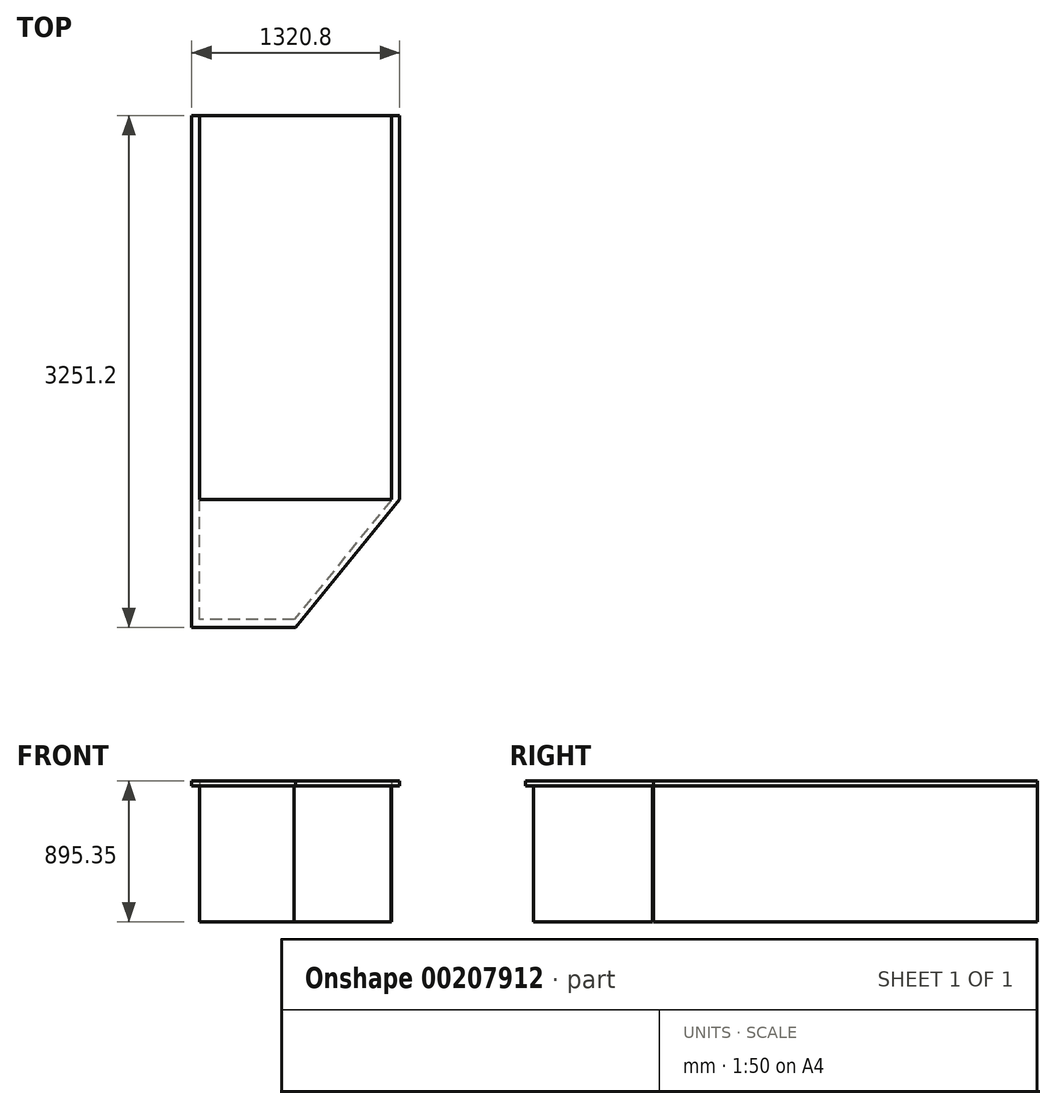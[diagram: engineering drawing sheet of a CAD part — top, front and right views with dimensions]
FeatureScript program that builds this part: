
annotation { "Feature Type Name" : "Feature", "Feature Type Description" : "" }
export const myFeature = defineFeature(function(context is Context, id is Id, definition is map)
    precondition{}
    {
        {
            var Q0;
            Q0=qCreatedBy(makeId("Top.planeOp"),FACE);
            var sketch = newSketch(context, id + "F0", { "sketchPlane" : qUnion([Q0])});
            skLineSegment(sketch, "E0.bottom", {"start": v(0, 0) * mm, "end": v(-1219.2, 0) * mm});
            skLineSegment(sketch, "E0.top", {"start": v(0, -2438.4) * mm, "end": v(-1219.2, -2438.4) * mm});
            skLineSegment(sketch, "E0.left", {"start": v(0, 0) * mm, "end": v(0, -2438.4) * mm});
            skLineSegment(sketch, "E0.right", {"start": v(-1219.2, 0) * mm, "end": v(-1219.2, -2438.4) * mm});
            skSolve(sketch);
        }
        {
            var Q0;
            Q0=makeQuery(id+"F0.imprint","IMPRINT",FACE,{"disambiguationData":[TD([[makeQuery(id+"F0.imprint","IMPRINT",EDGE,{"derivedFrom":sQuery(id+"F0.wireOp",EDGE,"E0.bottom")}),1.0]])]});
            extrude(context, id + "F1", {"entities" : qUnion([Q0]), "depth" : 863.6 * mm});
        }
        {
            var Q0;
            Q0=makeQuery(id+"F1.opExtrude","CAP_FACE",FACE,{"disambiguationData":[OSD([sQuery(id+"F0.wireOp",EDGE,"E0.bottom"),sQuery(id+"F0.wireOp",EDGE,"E0.top"),sQuery(id+"F0.wireOp",EDGE,"E0.left"),sQuery(id+"F0.wireOp",EDGE,"E0.right")])],"isStart":false});
            var sketch = newSketch(context, id + "F2", { "sketchPlane" : qUnion([Q0])});
            skLineSegment(sketch, "E1.bottom", {"start": v(-1270, 0) * mm, "end": v(50.8, 0) * mm});
            skLineSegment(sketch, "E1.top", {"start": v(-1270, -2438.4) * mm, "end": v(50.8, -2438.4) * mm});
            skLineSegment(sketch, "E1.left", {"start": v(-1270, 0) * mm, "end": v(-1270, -2438.4) * mm});
            skLineSegment(sketch, "E1.right", {"start": v(50.8, 0) * mm, "end": v(50.8, -2438.4) * mm});
            skLineSegment(sketch, "E2", {"start": v(-1270, -2438.4) * mm, "end": v(-1270, -3251.2) * mm});
            skLineSegment(sketch, "E3", {"start": v(-1270, -3251.2) * mm, "end": v(-609.6, -3251.2) * mm});
            skPoint(sketch, "E3.endSnap0", {"position": v(-609.6, -2438.4) * mm});
            skLineSegment(sketch, "E4", {"start": v(-609.6, -3251.2) * mm, "end": v(50.8, -2438.4) * mm});
            skSolve(sketch);
        }
        {
            var Q0;
            Q0=makeQuery(id+"F2.imprint","IMPRINT",FACE,{"disambiguationData":[TD([[makeQuery(id+"F2.imprint","IMPRINT",EDGE,{"derivedFrom":sQuery(id+"F2.wireOp",EDGE,"E1.top")}),1.0]])]});
            var Q1;
            Q1=makeQuery(id+"F2.imprint","IMPRINT",FACE,{"disambiguationData":[TD([[makeQuery(id+"F2.imprint","IMPRINT",EDGE,{"derivedFrom":makeQuery(id+"F1.opExtrude","CAP_EDGE",EDGE,{"disambiguationData":[OSD([sQuery(id+"F0.wireOp",EDGE,"E0.top")])],"isStart":false})}),-1.0]])]});
            var Q2;
            Q2=makeQuery(id+"F2.imprint","IMPRINT",FACE,{"disambiguationData":[TD([[makeQuery(id+"F2.imprint","IMPRINT",EDGE,{"derivedFrom":sQuery(id+"F2.wireOp",EDGE,"E1.top")}),-1.0]])]});
            extrude(context, id + "F3", {"entities" : qUnion([Q0, Q1, Q2]), "operationType" : NewBodyOperationType.ADD, "depth" : 31.75 * mm});
        }
        {
            var Q0;
            {var subQ4=sQuery(id+"F2.wireOp",EDGE,"E2");Q0=makeQuery(id+"F2.imprint","IMPRINT",FACE,{"disambiguationData":[TD([[makeQuery(id+"F2.imprint","IMPRINT",EDGE,{"derivedFrom":subQ4}),1.0]])]});}
            var sketch = newSketch(context, id + "F4", { "sketchPlane" : qUnion([Q0])});
            skLineSegment(sketch, "E5", {"start": v(0, -2438.4) * mm, "end": v(-619.12, -3200.4) * mm});
            skLineSegment(sketch, "E6", {"start": v(-619.12, -3200.4) * mm, "end": v(-1219.2, -3200.4) * mm});
            skLineSegment(sketch, "E7", {"start": v(-1219.2, -3200.4) * mm, "end": v(-1219.2, -2438.4) * mm});
            skLineSegment(sketch, "E8", {"start": v(-1219.2, -2438.4) * mm, "end": v(0, -2438.4) * mm});
            skLineSegment(sketch, "E9.0", {"start": v(0, -2444.75) * mm, "end": v(-1219.2, -2444.75) * mm});
            skLineSegment(sketch, "E9.1", {"start": v(-1263.65, -2444.75) * mm, "end": v(-1263.65, -3244.85) * mm});
            skLineSegment(sketch, "E9.2", {"start": v(-1263.65, -3244.85) * mm, "end": v(-612.62, -3244.85) * mm});
            skLineSegment(sketch, "E9.3", {"start": v(-1219.2, -2444.75) * mm, "end": v(-1263.65, -2444.75) * mm});
            skLineSegment(sketch, "E9.4", {"start": v(-612.62, -3244.85) * mm, "end": v(37.46, -2444.75) * mm});
            skLineSegment(sketch, "E9.5", {"start": v(37.46, -2444.75) * mm, "end": v(0, -2444.75) * mm});
            skSolve(sketch);
        }
        {
            var Q0;
            {var subQ1=makeQuery(id+"F1.opExtrude","CAP_EDGE",EDGE,{"disambiguationData":[OSD([sQuery(id+"F0.wireOp",EDGE,"E0.left")])],"isStart":false});Q0=makeQuery(id+"F2.imprint","IMPRINT",FACE,{"disambiguationData":[TD([[makeQuery(id+"F2.imprint","IMPRINT",EDGE,{"derivedFrom":subQ1}),-1.0]])]});}
            extrude(context, id + "F5", {"entities" : qUnion([Q0]), "depth" : 31.75 * mm});
        }
        {
            var Q0;
            {var subQ0=sQuery(id+"F4.wireOp",EDGE,"E6");Q0=makeQuery(id+"F4.imprint","IMPRINT",FACE,{"disambiguationData":[TD([[makeQuery(id+"F4.imprint","IMPRINT",EDGE,{"derivedFrom":subQ0}),-1.0]])]});}
            extrude(context, id + "F6", {"entities" : qUnion([Q0]), "operationType" : NewBodyOperationType.ADD, "oppositeDirection" : true, "depth" : 863.6 * mm});
        }
    });
